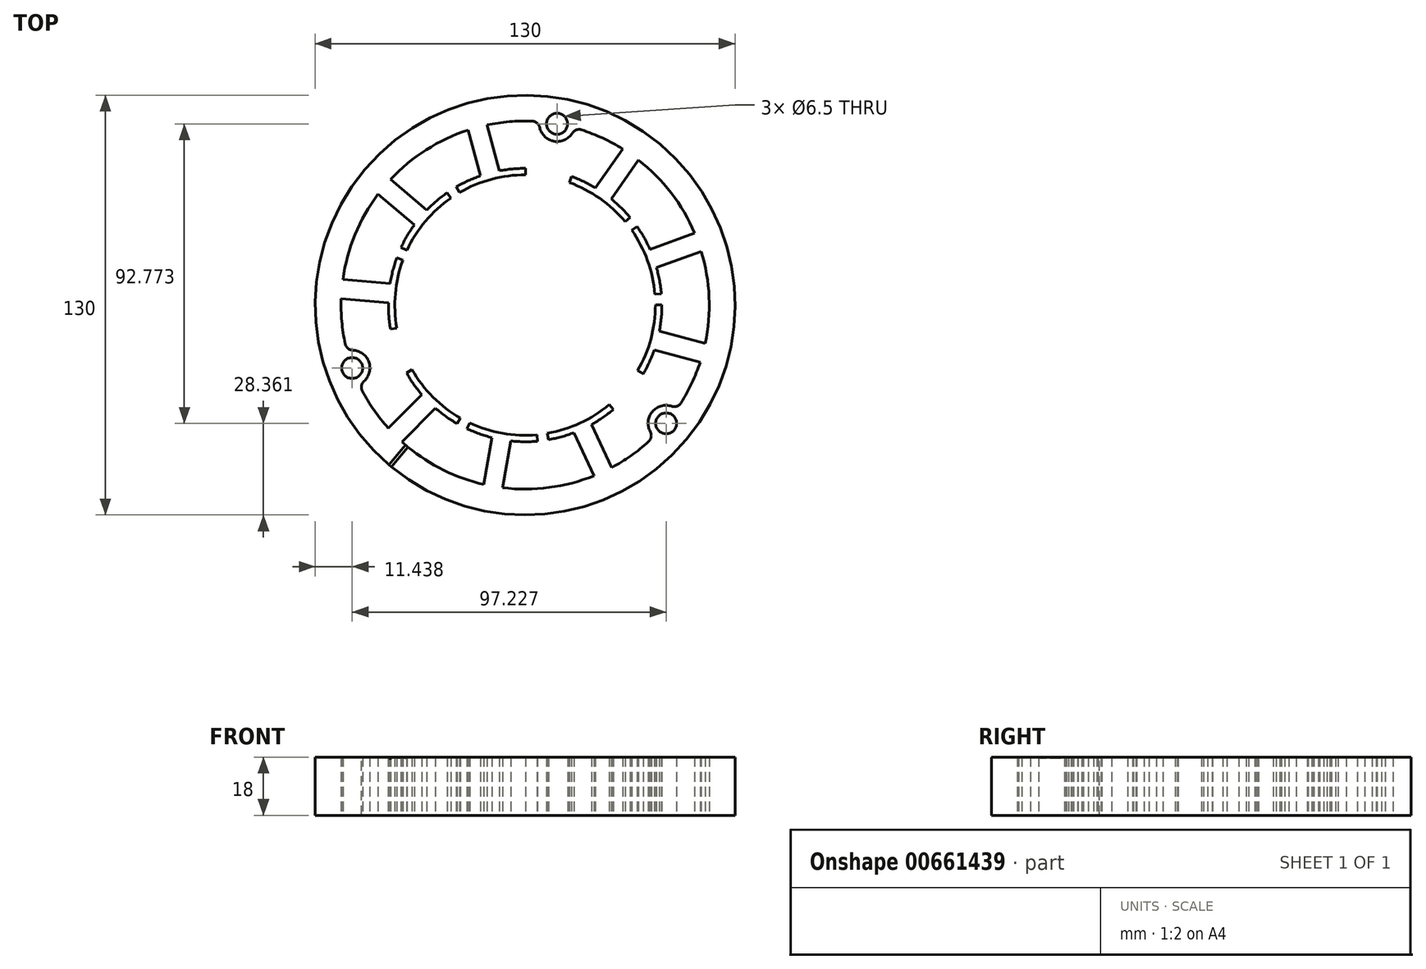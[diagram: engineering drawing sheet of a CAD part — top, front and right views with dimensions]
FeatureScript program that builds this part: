
annotation { "Feature Type Name" : "Feature", "Feature Type Description" : "" }
export const myFeature = defineFeature(function(context is Context, id is Id, definition is map)
    precondition{}
    {
        {
            var Q0;
            Q0=qCreatedBy(makeId("Top.planeOp"),FACE);
            var sketch = newSketch(context, id + "F0", { "sketchPlane" : qUnion([Q0])});
            skCircle(sketch, "E0", {"center": v(0, 0) * mm, "radius": 65 * mm});
            skCircle(sketch, "E1", {"center": v(0, 0) * mm, "radius": 57 * mm});
            skSolve(sketch);
        }
        {
            var Q0;
            Q0=makeQuery(id+"F0.imprint","IMPRINT",FACE,{"disambiguationData":[TD([[makeQuery(id+"F0.imprint","IMPRINT",EDGE,{"derivedFrom":sQuery(id+"F0.wireOp",EDGE,"E0")}),1.0]])]});
            extrude(context, id + "F1", {"entities" : qUnion([Q0]), "depth" : 18 * mm, "offsetDistance" : 25 * mm, "symmetric" : true});
        }
        {
            var Q0;
            Q0=qCreatedBy(makeId("Top.planeOp"),FACE);
            var sketch = newSketch(context, id + "F2", { "sketchPlane" : qUnion([Q0])});
            skCircle(sketch, "E2", {"center": v(-53.56, -19.5) * mm, "radius": 5.5 * mm});
            skCircle(sketch, "E3", {"center": v(9.9, 56.13) * mm, "radius": 5.5 * mm});
            skCircle(sketch, "E4", {"center": v(43.58, -36.57) * mm, "radius": 5.5 * mm});
            skSolve(sketch);
        }
        {
            var Q0;
            Q0=makeQuery(id+"F2.imprint","IMPRINT",FACE,{"disambiguationData":[TD([[makeQuery(id+"F2.imprint","IMPRINT",EDGE,{"derivedFrom":sQuery(id+"F2.wireOp",EDGE,"E2")}),1.0]])]});
            var Q1;
            Q1=makeQuery(id+"F2.imprint","IMPRINT",FACE,{"disambiguationData":[TD([[makeQuery(id+"F2.imprint","IMPRINT",EDGE,{"derivedFrom":sQuery(id+"F2.wireOp",EDGE,"E3")}),1.0]])]});
            var Q2;
            Q2=makeQuery(id+"F2.imprint","IMPRINT",FACE,{"disambiguationData":[TD([[makeQuery(id+"F2.imprint","IMPRINT",EDGE,{"derivedFrom":sQuery(id+"F2.wireOp",EDGE,"E4")}),1.0]])]});
            extrude(context, id + "F3", {"entities" : qUnion([Q0, Q1, Q2]), "operationType" : NewBodyOperationType.ADD, "depth" : 18 * mm, "offsetDistance" : 25 * mm, "symmetric" : true});
        }
        {
            var Q0;
            Q0=makeQuery(id+"F3.boolean.opBoolean","INTERSECT",EDGE,{"disambiguationData":[OD(1.0)],"derivedFrom":[makeQuery(id+"F1.opExtrude","SWEPT_FACE",FACE,{"disambiguationData":[OSD([sQuery(id+"F0.wireOp",EDGE,"E1")])]}),makeQuery(id+"F3.opExtrude","SWEPT_FACE",FACE,{"disambiguationData":[OSD([sQuery(id+"F2.wireOp",EDGE,"E2")])]})]});
            var Q1;
            Q1=makeQuery(id+"F3.boolean.opBoolean","INTERSECT",EDGE,{"disambiguationData":[OD(1.0)],"derivedFrom":[makeQuery(id+"F1.opExtrude","SWEPT_FACE",FACE,{"disambiguationData":[OSD([sQuery(id+"F0.wireOp",EDGE,"E1")])]}),makeQuery(id+"F3.opExtrude","SWEPT_FACE",FACE,{"disambiguationData":[OSD([sQuery(id+"F2.wireOp",EDGE,"E3")])]})]});
            var Q2;
            Q2=makeQuery(id+"F3.boolean.opBoolean","INTERSECT",EDGE,{"disambiguationData":[OD(0.0)],"derivedFrom":[makeQuery(id+"F1.opExtrude","SWEPT_FACE",FACE,{"disambiguationData":[OSD([sQuery(id+"F0.wireOp",EDGE,"E1")])]}),makeQuery(id+"F3.opExtrude","SWEPT_FACE",FACE,{"disambiguationData":[OSD([sQuery(id+"F2.wireOp",EDGE,"E2")])]})]});
            var Q3;
            Q3=makeQuery(id+"F3.boolean.opBoolean","INTERSECT",EDGE,{"disambiguationData":[OD(0.0)],"derivedFrom":[makeQuery(id+"F1.opExtrude","SWEPT_FACE",FACE,{"disambiguationData":[OSD([sQuery(id+"F0.wireOp",EDGE,"E1")])]}),makeQuery(id+"F3.opExtrude","SWEPT_FACE",FACE,{"disambiguationData":[OSD([sQuery(id+"F2.wireOp",EDGE,"E3")])]})]});
            var Q4;
            Q4=makeQuery(id+"F3.boolean.opBoolean","INTERSECT",EDGE,{"disambiguationData":[OD(1.0)],"derivedFrom":[makeQuery(id+"F1.opExtrude","SWEPT_FACE",FACE,{"disambiguationData":[OSD([sQuery(id+"F0.wireOp",EDGE,"E1")])]}),makeQuery(id+"F3.opExtrude","SWEPT_FACE",FACE,{"disambiguationData":[OSD([sQuery(id+"F2.wireOp",EDGE,"E4")])]})]});
            var Q5;
            Q5=makeQuery(id+"F3.boolean.opBoolean","INTERSECT",EDGE,{"disambiguationData":[OD(0.0)],"derivedFrom":[makeQuery(id+"F1.opExtrude","SWEPT_FACE",FACE,{"disambiguationData":[OSD([sQuery(id+"F0.wireOp",EDGE,"E1")])]}),makeQuery(id+"F3.opExtrude","SWEPT_FACE",FACE,{"disambiguationData":[OSD([sQuery(id+"F2.wireOp",EDGE,"E4")])]})]});
            fillet(context, id + "F4", {"entities" : qUnion([Q0, Q1, Q2, Q3, Q4, Q5]), "radius" : 2.5 * mm, "tangentPropagation" : true, "allowEdgeOverflow" : false});
        }
        {
            var Q0;
            Q0=qCreatedBy(makeId("Top.planeOp"),FACE);
            var sketch = newSketch(context, id + "F5", { "sketchPlane" : qUnion([Q0])});
            skCircle(sketch, "E5", {"center": v(-53.56, -19.5) * mm, "radius": 3.25 * mm});
            skCircle(sketch, "E6", {"center": v(9.9, 56.13) * mm, "radius": 3.25 * mm});
            skCircle(sketch, "E7", {"center": v(43.66, -36.64) * mm, "radius": 3.25 * mm});
            skSolve(sketch);
        }
        {
            var Q0;
            Q0 = qSketchRegion(id + "F5", true);
            extrude(context, id + "F6", {"entities" : qUnion([Q0]), "operationType" : NewBodyOperationType.REMOVE, "endBound" : BoundingType.UP_TO_NEXT, "depth" : 25 * mm, "offsetDistance" : 25 * mm, "hasSecondDirection" : true, "secondDirectionBound" : BoundingType.UP_TO_NEXT, "secondDirectionOppositeDirection" : true, "secondDirectionDepth" : 25 * mm});
        }
        {
            var Q0;
            Q0=qCreatedBy(makeId("Top.planeOp"),FACE);
            var sketch = newSketch(context, id + "F7", { "sketchPlane" : qUnion([Q0])});
            skArc(sketch, "E8", {"start": v(-37.85, 13.92) * mm, "mid": v(-40.18, 3.52) * mm, "end": v(-39.72, -7.12) * mm});
            skLineSegment(sketch, "E9.right", {"start": v(-57.25, 2) * mm, "end": v(-56.72, 7.98) * mm});
            skArc(sketch, "E10", {"start": v(-39.72, 14.61) * mm, "mid": v(-40.96, 10.7) * mm, "end": v(-41.8, 6.67) * mm});
            skLineSegment(sketch, "E11.trimOffspring", {"start": v(-41.8, 6.67) * mm, "end": v(-56.72, 7.98) * mm});
            skArc(sketch, "E12.trimOffspring", {"start": v(-42.34, 0.7) * mm, "mid": v(-42.21, -3.4) * mm, "end": v(-41.69, -7.48) * mm});
            skLineSegment(sketch, "E13.trimOffspring", {"start": v(-42.34, 0.7) * mm, "end": v(-57.25, 2) * mm});
            skLineSegment(sketch, "E14", {"start": v(-39.72, -7.12) * mm, "end": v(-41.69, -7.48) * mm});
            skLineSegment(sketch, "E15", {"start": v(-39.72, 14.61) * mm, "end": v(-37.85, 13.92) * mm});
            skArc(sketch, "E16", {"start": v(-23.02, 33.11) * mm, "mid": v(-30.9, 25.94) * mm, "end": v(-36.62, 16.95) * mm});
            skLineSegment(sketch, "E17.right", {"start": v(-45.74, 34.48) * mm, "end": v(-41.89, 39.07) * mm});
            skArc(sketch, "E18", {"start": v(-24.16, 34.76) * mm, "mid": v(-27.42, 32.25) * mm, "end": v(-30.42, 29.44) * mm});
            skLineSegment(sketch, "E19.trimOffspring", {"start": v(-30.42, 29.44) * mm, "end": v(-41.89, 39.07) * mm});
            skArc(sketch, "E20.trimOffspring", {"start": v(-34.28, 24.85) * mm, "mid": v(-36.53, 21.42) * mm, "end": v(-38.44, 17.79) * mm});
            skLineSegment(sketch, "E21.trimOffspring", {"start": v(-34.28, 24.85) * mm, "end": v(-45.74, 34.48) * mm});
            skLineSegment(sketch, "E22", {"start": v(-36.62, 16.95) * mm, "end": v(-38.44, 17.79) * mm});
            skLineSegment(sketch, "E23", {"start": v(-24.16, 34.76) * mm, "end": v(-23.02, 33.11) * mm});
            skArc(sketch, "E24", {"start": v(0.14, 40.33) * mm, "mid": v(-10.43, 38.96) * mm, "end": v(-20.28, 34.89) * mm});
            skLineSegment(sketch, "E25.right", {"start": v(-17.7, 54.48) * mm, "end": v(-11.9, 56.03) * mm});
            skArc(sketch, "E26", {"start": v(0.15, 42.33) * mm, "mid": v(-3.96, 42.14) * mm, "end": v(-8.03, 41.57) * mm});
            skLineSegment(sketch, "E27.trimOffspring", {"start": v(-8.03, 41.57) * mm, "end": v(-11.9, 56.03) * mm});
            skArc(sketch, "E28.trimOffspring", {"start": v(-13.83, 40.02) * mm, "mid": v(-17.64, 38.5) * mm, "end": v(-21.28, 36.62) * mm});
            skLineSegment(sketch, "E29.trimOffspring", {"start": v(-13.83, 40.02) * mm, "end": v(-17.7, 54.48) * mm});
            skLineSegment(sketch, "E30", {"start": v(-20.28, 34.89) * mm, "end": v(-21.28, 36.62) * mm});
            skLineSegment(sketch, "E31", {"start": v(0.15, 42.33) * mm, "end": v(0.14, 40.33) * mm});
            skArc(sketch, "E32", {"start": v(30.97, 25.8) * mm, "mid": v(23.13, 33.02) * mm, "end": v(13.68, 37.95) * mm});
            skLineSegment(sketch, "E33.right", {"start": v(30.35, 48.56) * mm, "end": v(35.26, 45.12) * mm});
            skArc(sketch, "E34", {"start": v(32.5, 27.08) * mm, "mid": v(29.73, 30.1) * mm, "end": v(26.67, 32.85) * mm});
            skLineSegment(sketch, "E35.trimOffspring", {"start": v(26.67, 32.85) * mm, "end": v(35.26, 45.12) * mm});
            skArc(sketch, "E36.trimOffspring", {"start": v(21.76, 36.3) * mm, "mid": v(18.14, 38.24) * mm, "end": v(14.36, 39.82) * mm});
            skLineSegment(sketch, "E37.trimOffspring", {"start": v(21.76, 36.3) * mm, "end": v(30.35, 48.56) * mm});
            skLineSegment(sketch, "E38", {"start": v(13.68, 37.95) * mm, "end": v(14.36, 39.82) * mm});
            skLineSegment(sketch, "E39", {"start": v(32.5, 27.08) * mm, "end": v(30.97, 25.8) * mm});
            skArc(sketch, "E40", {"start": v(40.17, 3.36) * mm, "mid": v(37.9, 13.77) * mm, "end": v(32.98, 23.23) * mm});
            skLineSegment(sketch, "E41.right", {"start": v(52.72, 22.36) * mm, "end": v(54.77, 16.72) * mm});
            skArc(sketch, "E42", {"start": v(42.17, 3.53) * mm, "mid": v(41.63, 7.6) * mm, "end": v(40.7, 11.6) * mm});
            skLineSegment(sketch, "E43.trimOffspring", {"start": v(40.7, 11.6) * mm, "end": v(54.77, 16.72) * mm});
            skArc(sketch, "E44.trimOffspring", {"start": v(38.65, 17.24) * mm, "mid": v(36.8, 20.9) * mm, "end": v(34.6, 24.38) * mm});
            skLineSegment(sketch, "E45.trimOffspring", {"start": v(38.65, 17.24) * mm, "end": v(52.72, 22.36) * mm});
            skLineSegment(sketch, "E46", {"start": v(32.98, 23.23) * mm, "end": v(34.6, 24.38) * mm});
            skLineSegment(sketch, "E47", {"start": v(42.17, 3.53) * mm, "end": v(40.17, 3.36) * mm});
            skArc(sketch, "E48", {"start": v(34.84, -20.3) * mm, "mid": v(38.95, -10.47) * mm, "end": v(40.34, 0.1) * mm});
            skLineSegment(sketch, "E49.right", {"start": v(56.02, -11.93) * mm, "end": v(54.46, -17.72) * mm});
            skArc(sketch, "E50", {"start": v(36.57, -21.3) * mm, "mid": v(38.47, -17.66) * mm, "end": v(40, -13.85) * mm});
            skLineSegment(sketch, "E51.trimOffspring", {"start": v(40, -13.85) * mm, "end": v(54.46, -17.72) * mm});
            skArc(sketch, "E52.trimOffspring", {"start": v(41.56, -8.05) * mm, "mid": v(42.15, -4) * mm, "end": v(42.34, 0.1) * mm});
            skLineSegment(sketch, "E53.trimOffspring", {"start": v(41.56, -8.05) * mm, "end": v(56.02, -11.93) * mm});
            skLineSegment(sketch, "E54", {"start": v(40.34, 0.1) * mm, "end": v(42.34, 0.1) * mm});
            skLineSegment(sketch, "E55", {"start": v(36.57, -21.3) * mm, "end": v(34.84, -20.3) * mm});
            skArc(sketch, "E56", {"start": v(6.86, -39.72) * mm, "mid": v(17.03, -36.54) * mm, "end": v(26.02, -30.82) * mm});
            skLineSegment(sketch, "E57.right", {"start": v(26.88, -50.56) * mm, "end": v(21.44, -53.1) * mm});
            skArc(sketch, "E58", {"start": v(7.2, -41.7) * mm, "mid": v(11.2, -40.8) * mm, "end": v(15.12, -39.52) * mm});
            skLineSegment(sketch, "E59.trimOffspring", {"start": v(15.12, -39.52) * mm, "end": v(21.44, -53.1) * mm});
            skArc(sketch, "E60.trimOffspring", {"start": v(20.56, -37) * mm, "mid": v(24.05, -34.83) * mm, "end": v(27.3, -32.35) * mm});
            skLineSegment(sketch, "E61.trimOffspring", {"start": v(20.56, -37) * mm, "end": v(26.88, -50.56) * mm});
            skLineSegment(sketch, "E62", {"start": v(26.02, -30.82) * mm, "end": v(27.3, -32.35) * mm});
            skLineSegment(sketch, "E63", {"start": v(7.2, -41.7) * mm, "end": v(6.86, -39.72) * mm});
            skArc(sketch, "E64", {"start": v(-17.18, -36.47) * mm, "mid": v(-7.02, -39.7) * mm, "end": v(3.63, -40.17) * mm});
            skLineSegment(sketch, "E65.right", {"start": v(-7, -56.84) * mm, "end": v(-12.9, -55.8) * mm});
            skArc(sketch, "E66", {"start": v(-18.03, -38.28) * mm, "mid": v(-14.23, -39.85) * mm, "end": v(-10.3, -41.05) * mm});
            skLineSegment(sketch, "E67.trimOffspring", {"start": v(-10.3, -41.05) * mm, "end": v(-12.9, -55.8) * mm});
            skArc(sketch, "E68.trimOffspring", {"start": v(-4.4, -42.1) * mm, "mid": v(-0.3, -42.33) * mm, "end": v(3.8, -42.16) * mm});
            skLineSegment(sketch, "E69.trimOffspring", {"start": v(-4.4, -42.1) * mm, "end": v(-7, -56.84) * mm});
            skLineSegment(sketch, "E70", {"start": v(3.63, -40.17) * mm, "end": v(3.8, -42.16) * mm});
            skLineSegment(sketch, "E71", {"start": v(-18.03, -38.28) * mm, "end": v(-17.18, -36.47) * mm});
            skArc(sketch, "E72", {"start": v(-35, -20.02) * mm, "mid": v(-28.54, -28.5) * mm, "end": v(-20.08, -34.99) * mm});
            skLineSegment(sketch, "E73.right", {"start": v(-38.34, -42.55) * mm, "end": v(-42.58, -38.3) * mm});
            skArc(sketch, "E74", {"start": v(-36.74, -21.02) * mm, "mid": v(-34.53, -24.48) * mm, "end": v(-32, -27.72) * mm});
            skLineSegment(sketch, "E75.trimOffspring", {"start": v(-32, -27.72) * mm, "end": v(-42.58, -38.3) * mm});
            skArc(sketch, "E76.trimOffspring", {"start": v(-27.76, -31.97) * mm, "mid": v(-24.53, -34.5) * mm, "end": v(-21.08, -36.72) * mm});
            skLineSegment(sketch, "E77.trimOffspring", {"start": v(-27.76, -31.97) * mm, "end": v(-38.34, -42.55) * mm});
            skLineSegment(sketch, "E78", {"start": v(-20.08, -34.99) * mm, "end": v(-21.08, -36.72) * mm});
            skLineSegment(sketch, "E79", {"start": v(-36.74, -21.02) * mm, "end": v(-35, -20.02) * mm});
            skSolve(sketch);
        }
        {
            var Q0;
            Q0=qCreatedBy(makeId("Top.planeOp"),FACE);
            var sketch = newSketch(context, id + "F8", { "sketchPlane" : qUnion([Q0])});
            skLineSegment(sketch, "E80", {"start": v(0, 0) * mm, "end": v(-44.5, -53.04) * mm});
            skLineSegment(sketch, "E81", {"start": v(0, 0) * mm, "end": v(-72.52, 12.79) * mm});
            skLineSegment(sketch, "E82.bottom", {"start": v(-34.7, -40.57) * mm, "end": v(-44.34, -52.06) * mm});
            skLineSegment(sketch, "E82.top", {"start": v(-33.93, -41.22) * mm, "end": v(-43.57, -52.7) * mm});
            skLineSegment(sketch, "E82.left", {"start": v(-34.7, -40.57) * mm, "end": v(-33.93, -41.22) * mm});
            skLineSegment(sketch, "E82.right", {"start": v(-44.34, -52.06) * mm, "end": v(-43.57, -52.7) * mm});
            skPoint(sketch, "E82.middle", {"position": v(-39.14, -46.64) * mm});
            skSolve(sketch);
        }
        {
            var Q0;
            Q0 = qSketchRegion(id + "F8", true);
            extrude(context, id + "F9", {"entities" : qUnion([Q0]), "operationType" : NewBodyOperationType.REMOVE, "depth" : 25 * mm, "offsetDistance" : 25 * mm, "hasSecondDirection" : true, "secondDirectionOppositeDirection" : false, "secondDirectionDepth" : 8.6 * mm});
        }
        {
            var Q0;
            Q0 = qSketchRegion(id + "F7", true);
            extrude(context, id + "F10", {"entities" : qUnion([Q0]), "operationType" : NewBodyOperationType.ADD, "depth" : 18 * mm, "offsetDistance" : 25 * mm, "symmetric" : true});
        }
    });
